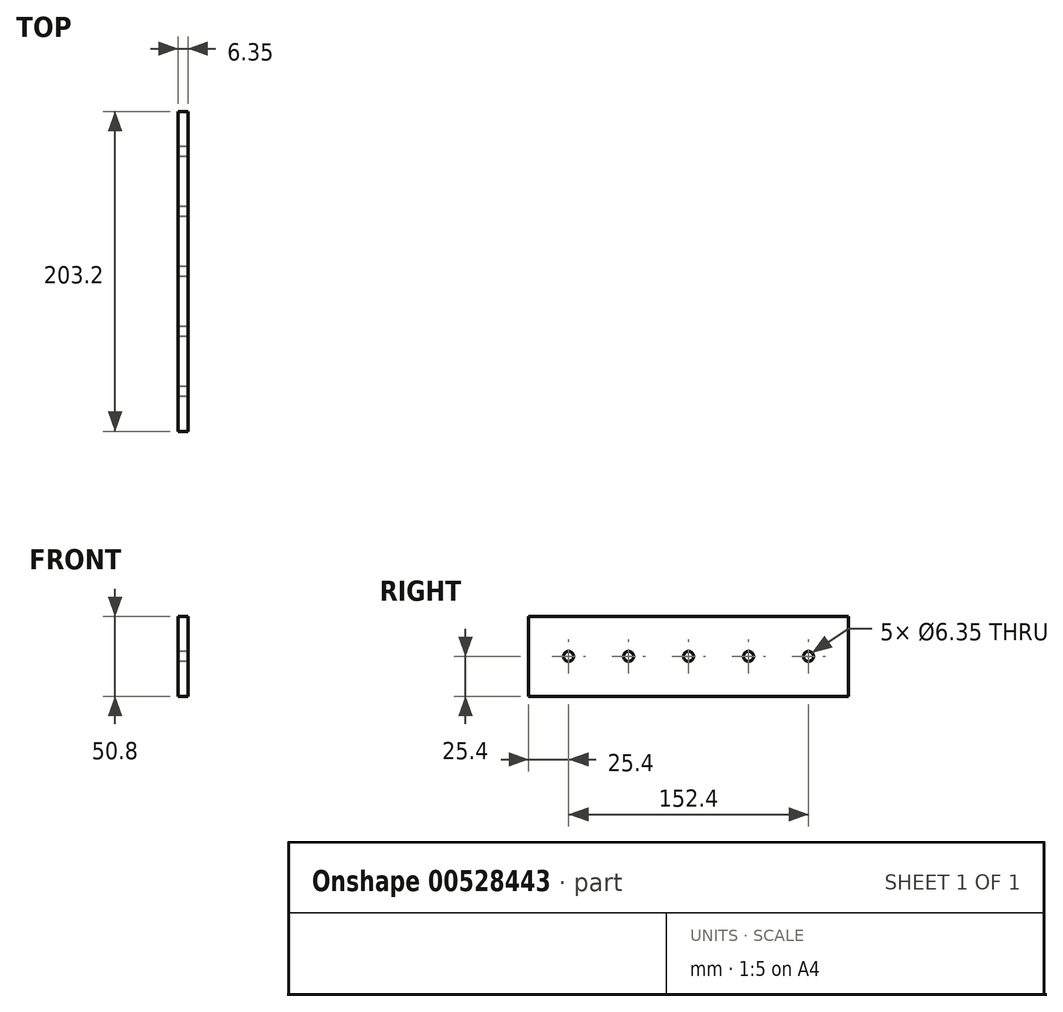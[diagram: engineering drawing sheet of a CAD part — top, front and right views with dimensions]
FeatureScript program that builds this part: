
annotation { "Feature Type Name" : "Feature", "Feature Type Description" : "" }
export const myFeature = defineFeature(function(context is Context, id is Id, definition is map)
    precondition{}
    {
        {
            var Q0;
            Q0=qCreatedBy(makeId("Right.planeOp"),FACE);
            var sketch = newSketch(context, id + "F0", { "sketchPlane" : qUnion([Q0])});
            skLineSegment(sketch, "E0", {"start": v(0, 0) * mm, "end": v(0, 25.4) * mm, "construction": true});
            skLineSegment(sketch, "E1.bottom", {"start": v(-101.6, 25.4) * mm, "end": v(101.6, 25.4) * mm});
            skLineSegment(sketch, "E1.top", {"start": v(-101.6, -25.4) * mm, "end": v(101.6, -25.4) * mm});
            skLineSegment(sketch, "E1.left", {"start": v(-101.6, 25.4) * mm, "end": v(-101.6, -25.4) * mm});
            skLineSegment(sketch, "E1.right", {"start": v(101.6, 25.4) * mm, "end": v(101.6, -25.4) * mm});
            skCircle(sketch, "E2", {"center": v(0, 0) * mm, "radius": 3.18 * mm});
            skCircle(sketch, "E3", {"center": v(-76.2, 0) * mm, "radius": 3.18 * mm});
            skCircle(sketch, "E4", {"center": v(76.2, 0) * mm, "radius": 3.18 * mm});
            skCircle(sketch, "E5", {"center": v(-38.1, 0) * mm, "radius": 6.35 * mm, "construction": true});
            skCircle(sketch, "E6", {"center": v(38.1, 0) * mm, "radius": 3.18 * mm});
            skCircle(sketch, "E7", {"center": v(0, 0) * mm, "radius": 31.75 * mm, "construction": true});
            skCircle(sketch, "E8", {"center": v(-76.2, 0) * mm, "radius": 31.75 * mm, "construction": true});
            skCircle(sketch, "E9", {"center": v(76.2, 0) * mm, "radius": 31.75 * mm, "construction": true});
            skCircle(sketch, "E10", {"center": v(-38.1, 0) * mm, "radius": 3.18 * mm});
            skCircle(sketch, "E11", {"center": v(38.1, 0) * mm, "radius": 6.35 * mm, "construction": true});
            skCircle(sketch, "E12", {"center": v(-38.1, 0) * mm, "radius": 9.53 * mm, "construction": true});
            skCircle(sketch, "E13", {"center": v(-76.2, 0) * mm, "radius": 28.58 * mm, "construction": true});
            skCircle(sketch, "E14", {"center": v(38.1, 0) * mm, "radius": 9.52 * mm, "construction": true});
            skCircle(sketch, "E15", {"center": v(76.2, 0) * mm, "radius": 28.58 * mm, "construction": true});
            skCircle(sketch, "E16", {"center": v(0, 0) * mm, "radius": 28.57 * mm, "construction": true});
            skSolve(sketch);
        }
        {
            var Q0;
            Q0 = qSketchRegion(id + "F0", true);
            extrude(context, id + "F1", {"entities" : qUnion([Q0]), "depth" : 6.35 * mm, "offsetDistance" : 25.4 * mm});
        }
    });
